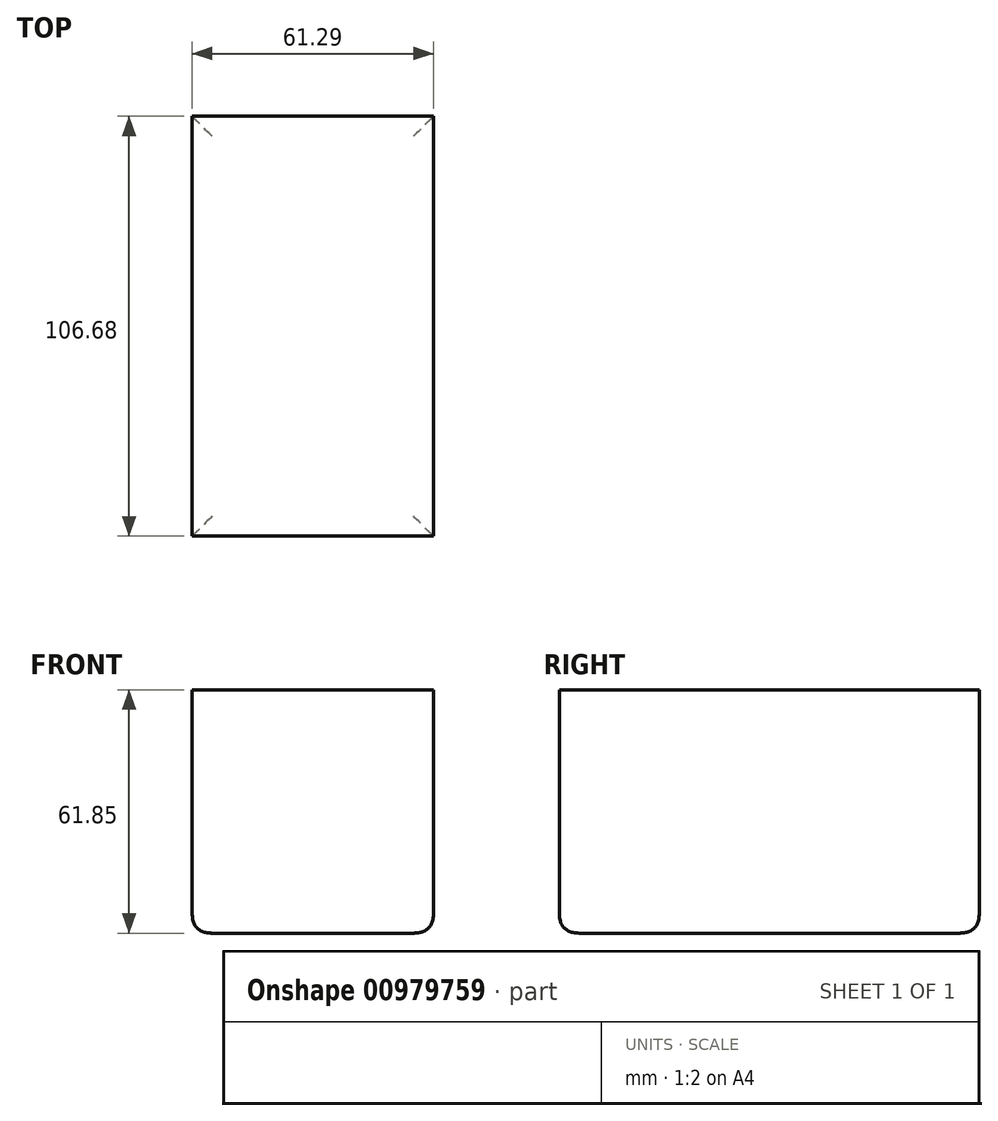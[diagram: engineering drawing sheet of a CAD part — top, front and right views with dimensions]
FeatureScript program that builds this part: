
annotation { "Feature Type Name" : "Feature", "Feature Type Description" : "" }
export const myFeature = defineFeature(function(context is Context, id is Id, definition is map)
    precondition{}
    {
        {
            var Q0;
            Q0=qCreatedBy(makeId("Front.planeOp"),FACE);
            var sketch = newSketch(context, id + "F0", { "sketchPlane" : qUnion([Q0])});
            skLineSegment(sketch, "E0.bottom", {"start": v(-123.72, 57.68) * mm, "end": v(-62.43, 57.68) * mm});
            skLineSegment(sketch, "E0.top", {"start": v(-123.72, -4.17) * mm, "end": v(-62.43, -4.17) * mm});
            skLineSegment(sketch, "E0.left", {"start": v(-123.72, 57.68) * mm, "end": v(-123.72, -4.17) * mm});
            skLineSegment(sketch, "E0.right", {"start": v(-62.43, 57.68) * mm, "end": v(-62.43, -4.17) * mm});
            skSolve(sketch);
        }
        {
            var Q0;
            Q0 = qSketchRegion(id + "F0", true);
            extrude(context, id + "F1", {"entities" : qUnion([Q0]), "depth" : 106.68 * mm, "offsetDistance" : 25.4 * mm});
        }
        {
            var Q0;
            Q0=makeQuery(id+"F1.opExtrude","SWEPT_EDGE",EDGE,{"disambiguationData":[OSD([sQuery(id+"F0.wireOp",EDGE,"E0.top"),sQuery(id+"F0.wireOp",EDGE,"E0.left")])]});
            var Q1;
            Q1=makeQuery(id+"F1.opExtrude","CAP_EDGE",EDGE,{"disambiguationData":[OSD([sQuery(id+"F0.wireOp",EDGE,"E0.top")])],"isStart":false});
            var Q2;
            Q2=makeQuery(id+"F1.opExtrude","SWEPT_EDGE",EDGE,{"disambiguationData":[OSD([sQuery(id+"F0.wireOp",EDGE,"E0.top"),sQuery(id+"F0.wireOp",EDGE,"E0.right")])]});
            var Q3;
            Q3=makeQuery(id+"F1.opExtrude","CAP_EDGE",EDGE,{"disambiguationData":[OSD([sQuery(id+"F0.wireOp",EDGE,"E0.top")])],"isStart":true});
            fillet(context, id + "F2", {"entities" : qUnion([Q0, Q1, Q2, Q3]), "radius" : 5.08 * mm, "tangentPropagation" : true, "rho" : 0.5, "crossSection" : FilletCrossSection.CONIC, "allowEdgeOverflow" : false});
        }
    });
